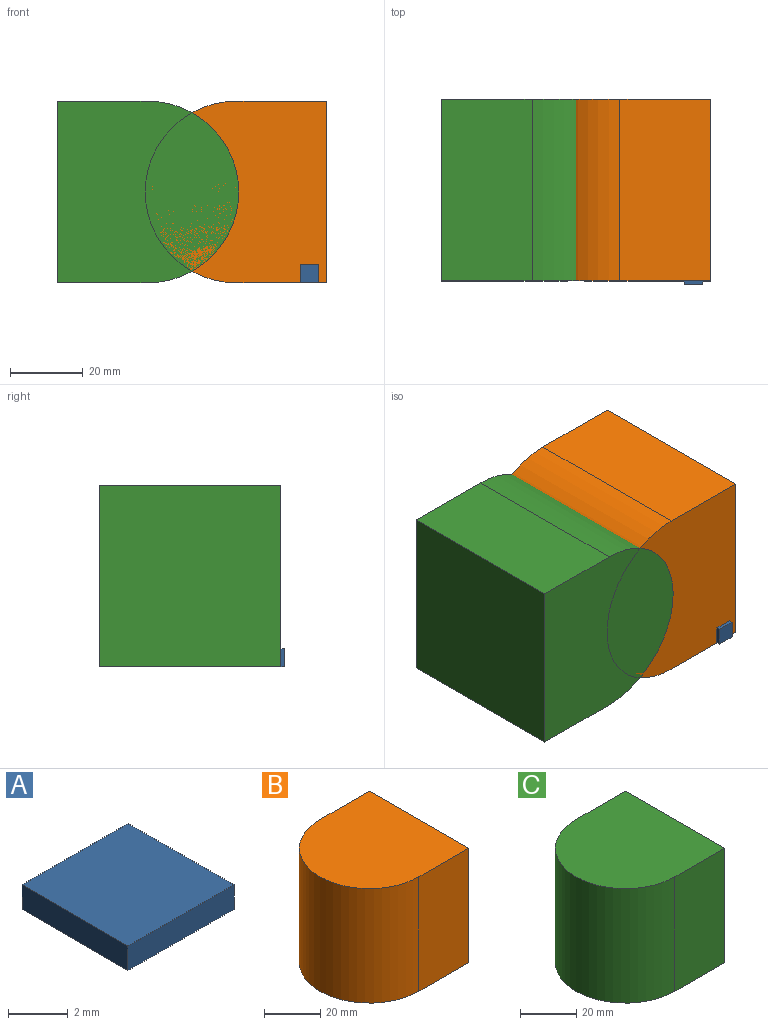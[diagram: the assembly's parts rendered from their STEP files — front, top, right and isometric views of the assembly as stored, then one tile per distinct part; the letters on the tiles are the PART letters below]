
ASSEMBLY  parts=3 mates=5
PART A: 6 faces, bbox 5x5x1 mm
  f0: plane 5x1mm, normal (0,-1,0), area 5mm2, adj f1,f3,f4,f5
  f1: plane 5x1mm, normal (1,0,0), area 5mm2, adj f0,f2,f4,f5
  f2: plane 5x1mm, normal (0,1,0), area 5mm2, adj f1,f3,f4,f5
  f3: plane 5x1mm, normal (-1,0,0), area 5mm2, adj f0,f2,f4,f5
  f4: plane 5x5mm, normal (0,0,1), area 25mm2, adj f0,f1,f2,f3
  f5: plane 5x5mm, normal (0,0,-1), area 25mm2, adj f0,f1,f2,f3
PART B: 6 faces, bbox 50x50x50 mm
  f0: plane 50x25mm, normal (0,-1,0), area 1250mm2, adj f1,f3,f4,f5
  f1: plane 50x50mm, normal (1,0,0), area 2500mm2, adj f0,f2,f4,f5
  f2: plane 50x25mm, normal (0,1,0), area 1250mm2, adj f1,f3,f4,f5
  f3: cylinder r=25mm len=50mm, axis (0,0,-1), area 3927mm2, adj f0,f2,f4,f5
  f4: plane 50x50mm, normal (0,0,1), area 2231.7mm2, adj f0,f1,f2,f3
  f5: plane 50x50mm, normal (0,0,-1), area 2231.7mm2, adj f0,f1,f2,f3
PART C: 6 faces, bbox 50x50x50 mm
  f0: plane 50x25mm, normal (0,-1,0), area 1250mm2, adj f1,f3,f4,f5
  f1: plane 50x50mm, normal (1,0,0), area 2500mm2, adj f0,f2,f4,f5
  f2: plane 50x25mm, normal (0,1,0), area 1250mm2, adj f1,f3,f4,f5
  f3: cylinder r=25mm len=50mm, axis (0,0,1), area 3927mm2, adj f0,f2,f4,f5
  f4: plane 50x50mm, normal (0,0,-1), area 2231.7mm2, adj f0,f1,f2,f3
  f5: plane 50x50mm, normal (0,0,1), area 2231.7mm2, adj f0,f1,f2,f3
PLACE A rot(axis=(-1,0,0),90deg) t=(-52.41,-63.08,-0.95)mm
PLACE B rot(axis=(1,0,0),90deg) t=(0,-12.08,19.05)mm
PLACE C rot(axis=(0,0.71,-0.71),180deg) t=(-24.23,-62.08,19.05)mm
MATE planar A.f4 <-> B.f4  axis (0,1,0) through (20.3,-62.08,-3.45)mm
MATE planar C.f2 <-> B.f0  axis (0,0,-1) through (-36.73,-37.08,-5.95)mm
MATE planar C.f5 <-> B.f4  axis (0,-1,0) through (-26.57,-62.08,19.05)mm
MATE planar A.f2 <-> B.f0  axis (0,0,-1) through (20.3,-62.58,-5.95)mm
MATE planar B.f4 <-> C.f5  axis (0,-1,0) through (2.33,-62.08,19.05)mm
